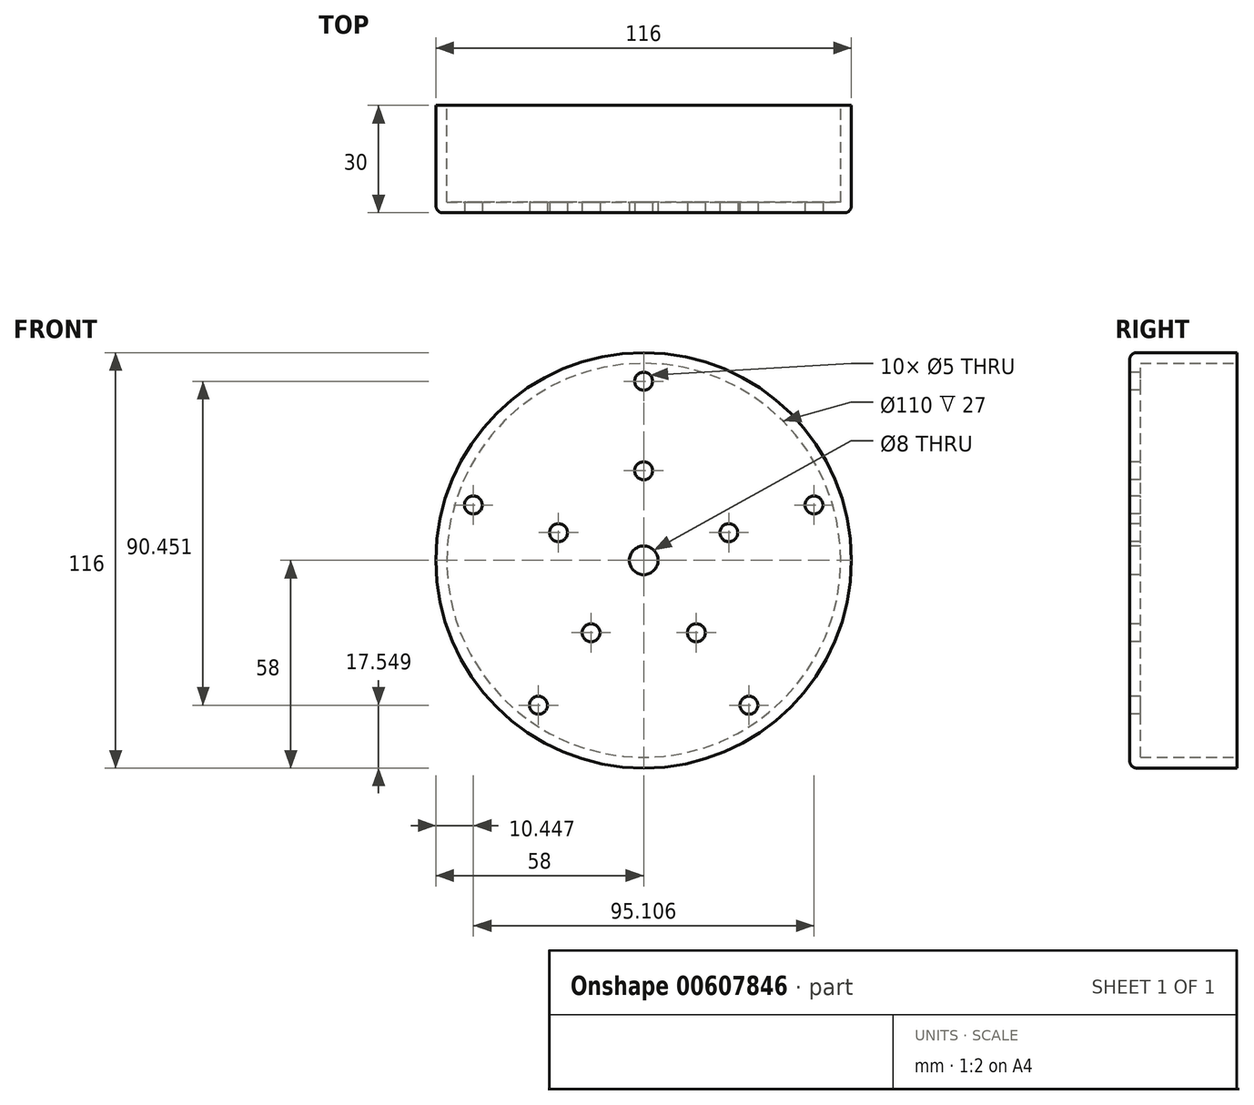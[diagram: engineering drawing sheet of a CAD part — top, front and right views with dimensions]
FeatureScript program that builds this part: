
annotation { "Feature Type Name" : "Feature", "Feature Type Description" : "" }
export const myFeature = defineFeature(function(context is Context, id is Id, definition is map)
    precondition{}
    {
        {
            var Q0;
            Q0=qCreatedBy(makeId("Front.planeOp"),FACE);
            var sketch = newSketch(context, id + "F0", { "sketchPlane" : qUnion([Q0])});
            skCircle(sketch, "E0", {"center": v(0, 0) * mm, "radius": 58 * mm});
            skSolve(sketch);
        }
        {
            var Q0;
            Q0=qSketchRegion(id+"F0",true);
            extrude(context, id + "F1", {"entities" : qUnion([Q0]), "depth" : 30 * mm});
        }
        {
            var Q0;
            Q0=makeQuery(id+"F1.opExtrude","CAP_FACE",FACE,{"disambiguationData":[OSD([sQuery(id+"F0.wireOp",EDGE,"E0")])],"isStart":true});
            shell(context, id + "F2", {"entities" : qUnion([Q0]), "thickness" : 3 * mm});
        }
        {
            var Q0;
            Q0=makeQuery(id+"F1.opExtrude","CAP_EDGE",EDGE,{"disambiguationData":[OSD([sQuery(id+"F0.wireOp",EDGE,"E0")])],"isStart":false});
            fillet(context, id + "F3", {"entities" : qUnion([Q0]), "radius" : 2 * mm, "tangentPropagation" : true, "allowEdgeOverflow" : false});
        }
        {
            var Q0;
            Q0=makeQuery(id+"F1.opExtrude","CAP_FACE",FACE,{"disambiguationData":[OSD([sQuery(id+"F0.wireOp",EDGE,"E0")])],"isStart":false});
            var sketch = newSketch(context, id + "F4", { "sketchPlane" : qUnion([Q0])});
            skPoint(sketch, "E1", {"position": v(0, 0) * mm});
            skSolve(sketch);
        }
        {
            var Q0;
            Q0=sQuery(id+"F4.wireOp",VERTEX,"E1");
            var Q1;
            Q1=makeQuery(id+"F1.opExtrude","SWEPT_BODY",BODY,{"disambiguationData":[OSD([sQuery(id+"F0.wireOp",EDGE,"E0")])]});
            hole(context, id + "F5", {"style" : HoleStyle.SIMPLE, "endStyle" : HoleEndStyle.THROUGH, "holeDiameter" : 8 * mm, "locations" : qUnion([Q0]), "scope" : qUnion([Q1]), "majorDiameter" : 5 * mm, "tappedDepth" : 12 * mm, "tapClearance" : 3});
        }
        {
            var Q0;
            Q0=makeQuery(id+"F1.opExtrude","CAP_FACE",FACE,{"disambiguationData":[OSD([sQuery(id+"F0.wireOp",EDGE,"E0")])],"isStart":false});
            var sketch = newSketch(context, id + "F6", { "sketchPlane" : qUnion([Q0])});
            skPoint(sketch, "E2", {"position": v(0, 25) * mm});
            skPoint(sketch, "E3", {"position": v(0, 50) * mm});
            skPoint(sketch, "E4.1.0", {"position": v(-47.55, 15.45) * mm});
            skPoint(sketch, "E4.1.1", {"position": v(-23.78, 7.73) * mm});
            skPoint(sketch, "E4.2.0", {"position": v(-29.39, -40.45) * mm});
            skPoint(sketch, "E4.2.1", {"position": v(-14.7, -20.23) * mm});
            skPoint(sketch, "E4.3.0", {"position": v(29.39, -40.45) * mm});
            skPoint(sketch, "E4.3.1", {"position": v(14.7, -20.23) * mm});
            skPoint(sketch, "E4.4.0", {"position": v(47.55, 15.45) * mm});
            skPoint(sketch, "E4.4.1", {"position": v(23.78, 7.73) * mm});
            skPoint(sketch, "E4.center", {"position": v(0, 0) * mm});
            skSolve(sketch);
        }
        {
            var Q0;
            Q0=sQuery(id+"F6.wireOp",VERTEX,"E2");
            var Q1;
            Q1=sQuery(id+"F6.wireOp",VERTEX,"E3");
            var Q2;
            Q2=sQuery(id+"F6.wireOp",VERTEX,"E4.1.1");
            var Q3;
            Q3=sQuery(id+"F6.wireOp",VERTEX,"E4.1.0");
            var Q4;
            Q4=sQuery(id+"F6.wireOp",VERTEX,"E4.2.0");
            var Q5;
            Q5=sQuery(id+"F6.wireOp",VERTEX,"E4.2.1");
            var Q6;
            Q6=sQuery(id+"F6.wireOp",VERTEX,"E4.3.1");
            var Q7;
            Q7=sQuery(id+"F6.wireOp",VERTEX,"E4.3.0");
            var Q8;
            Q8=sQuery(id+"F6.wireOp",VERTEX,"E4.4.1");
            var Q9;
            Q9=sQuery(id+"F6.wireOp",VERTEX,"E4.4.0");
            var Q10;
            Q10=makeQuery(id+"F1.opExtrude","SWEPT_BODY",BODY,{"disambiguationData":[OSD([sQuery(id+"F0.wireOp",EDGE,"E0")])]});
            hole(context, id + "F7", {"style" : HoleStyle.SIMPLE, "endStyle" : HoleEndStyle.THROUGH, "holeDiameter" : 5 * mm, "locations" : qUnion([Q0, Q1, Q2, Q3, Q4, Q5, Q6, Q7, Q8, Q9]), "scope" : qUnion([Q10]), "majorDiameter" : 5 * mm, "tappedDepth" : 12 * mm, "tapClearance" : 3});
        }
    });
